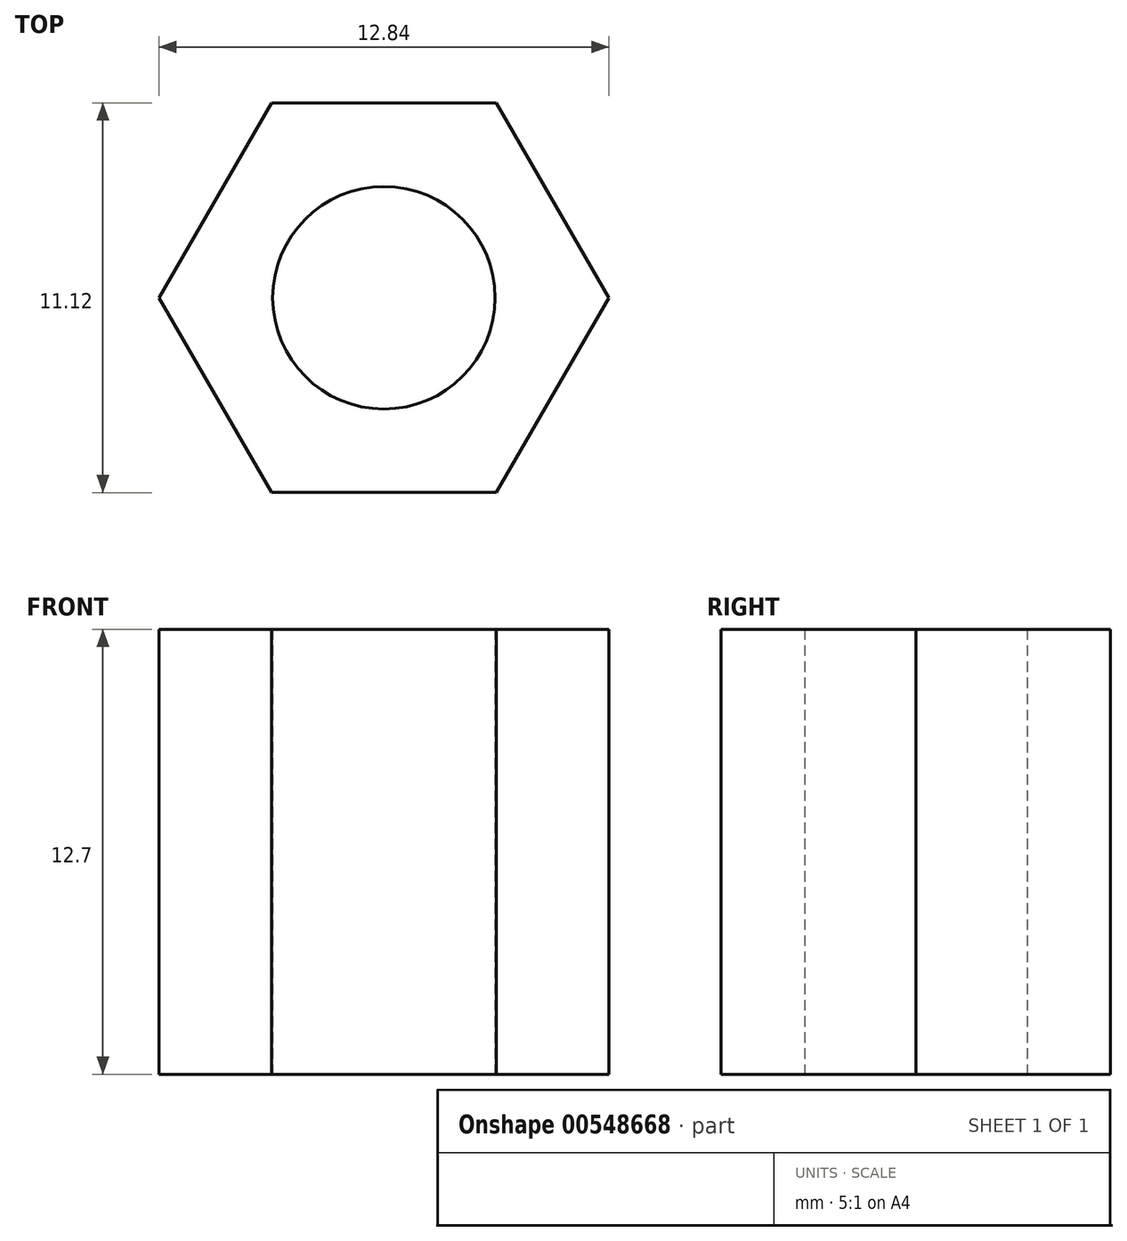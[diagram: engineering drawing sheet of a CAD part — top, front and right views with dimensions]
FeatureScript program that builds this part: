
annotation { "Feature Type Name" : "Feature", "Feature Type Description" : "" }
export const myFeature = defineFeature(function(context is Context, id is Id, definition is map)
    precondition{}
    {
        {
            var Q0;
            Q0=qCreatedBy(makeId("Top.planeOp"),FACE);
            var sketch = newSketch(context, id + "F0", { "sketchPlane" : qUnion([Q0])});
            skCircle(sketch, "E0.cCircle", {"center": v(0, 0) * mm, "radius": 5.56 * mm, "construction": true});
            skLineSegment(sketch, "E0.0", {"start": v(-3.2, 5.56) * mm, "end": v(3.2, 5.56) * mm});
            skLineSegment(sketch, "E0.1", {"start": v(3.2, 5.56) * mm, "end": v(6.42, 0) * mm});
            skLineSegment(sketch, "E0.2", {"start": v(6.42, 0) * mm, "end": v(3.2, -5.56) * mm});
            skLineSegment(sketch, "E0.3", {"start": v(3.2, -5.56) * mm, "end": v(-3.2, -5.56) * mm});
            skLineSegment(sketch, "E0.4", {"start": v(-3.2, -5.56) * mm, "end": v(-6.42, 0) * mm});
            skLineSegment(sketch, "E0.5", {"start": v(-6.42, 0) * mm, "end": v(-3.2, 5.56) * mm});
            skPoint(sketch, "E0.0.midPoint", {"position": v(0, 5.56) * mm});
            skCircle(sketch, "E1", {"center": v(0, 0) * mm, "radius": 3.18 * mm});
            skSolve(sketch);
        }
        {
            var Q0;
            Q0=makeQuery(id+"F0.imprint","IMPRINT",FACE,{"disambiguationData":[TD([[makeQuery(id+"F0.imprint","IMPRINT",EDGE,{"derivedFrom":sQuery(id+"F0.wireOp",EDGE,"E0.0")}),-1.0]])]});
            extrude(context, id + "F1", {"entities" : qUnion([Q0]), "endBound" : BoundingType.SYMMETRIC, "depth" : 12.7 * mm, "offsetDistance" : 25.4 * mm});
        }
    });
